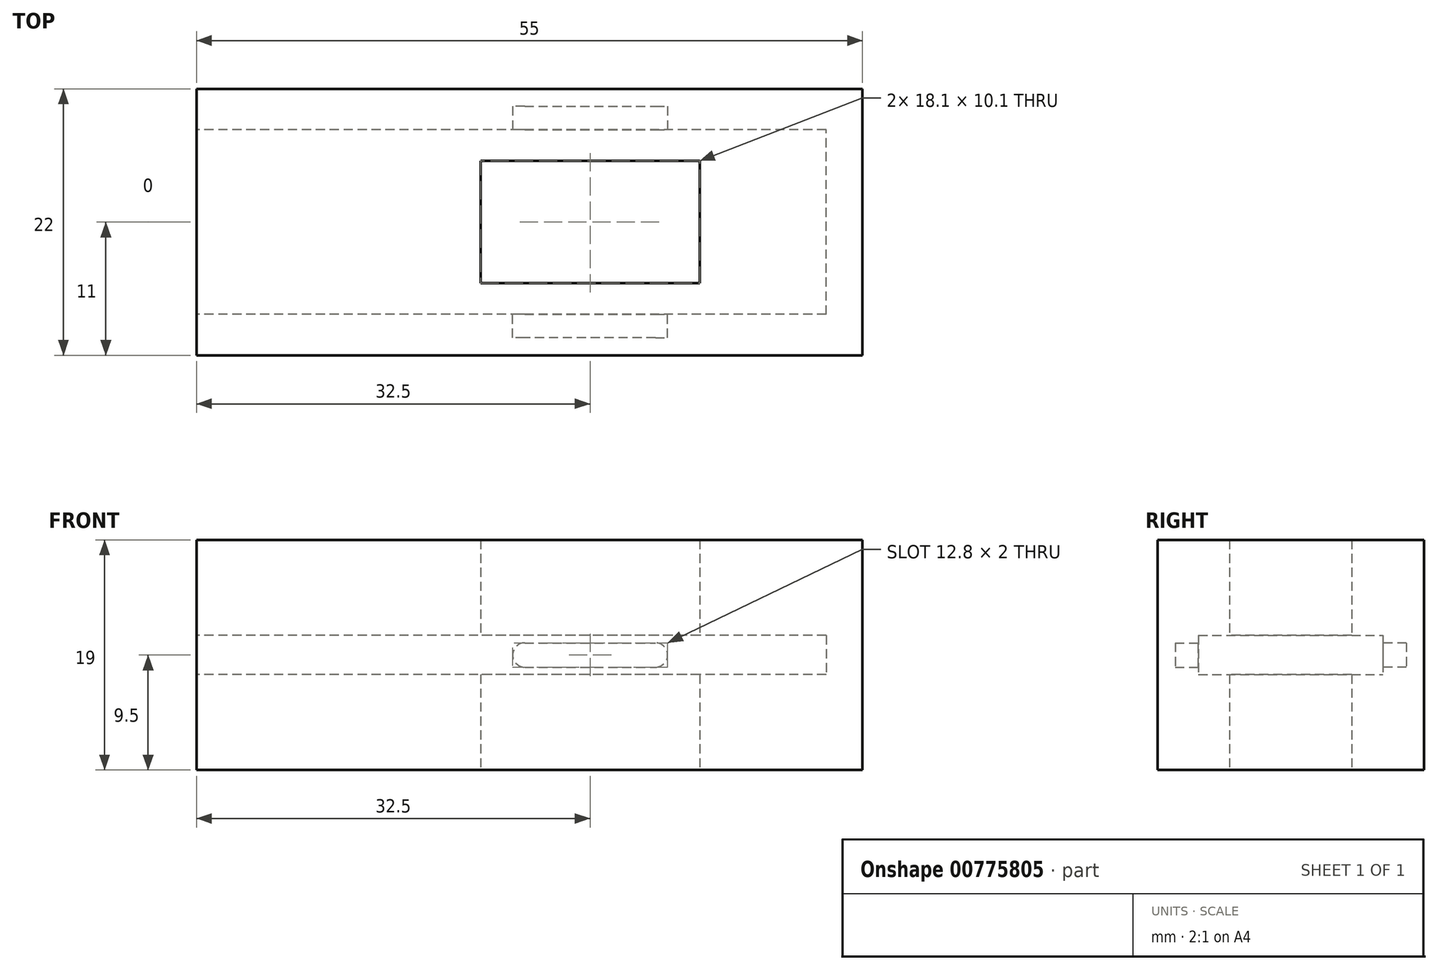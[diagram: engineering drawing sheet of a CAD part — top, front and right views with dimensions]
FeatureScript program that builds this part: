
annotation { "Feature Type Name" : "Feature", "Feature Type Description" : "" }
export const myFeature = defineFeature(function(context is Context, id is Id, definition is map)
    precondition{}
    {
        {
            var Q0;
            Q0=qCreatedBy(makeId("Front.planeOp"),FACE);
            var sketch = newSketch(context, id + "F0", { "sketchPlane" : qUnion([Q0])});
            skLineSegment(sketch, "E0.bottom", {"start": v(-27.5, 9.5) * mm, "end": v(27.5, 9.5) * mm});
            skLineSegment(sketch, "E0.top", {"start": v(-27.5, -9.5) * mm, "end": v(27.5, -9.5) * mm});
            skLineSegment(sketch, "E0.left", {"start": v(-27.5, 9.5) * mm, "end": v(-27.5, -9.5) * mm});
            skLineSegment(sketch, "E0.right", {"start": v(27.5, 9.5) * mm, "end": v(27.5, -9.5) * mm});
            skPoint(sketch, "E0.middle", {"position": v(0, 0) * mm});
            skPoint(sketch, "E1", {"position": v(5, 0) * mm});
            skSolve(sketch);
        }
        {
            var Q0;
            Q0=makeQuery(id+"F0.imprint","IMPRINT",FACE,{"disambiguationData":[TD([[makeQuery(id+"F0.imprint","IMPRINT",EDGE,{"derivedFrom":sQuery(id+"F0.wireOp",EDGE,"E0.bottom")}),-1.0]])]});
            extrude(context, id + "F1", {"entities" : qUnion([Q0]), "endBound" : BoundingType.SYMMETRIC, "depth" : 22 * mm, "offsetDistance" : 25 * mm});
        }
        {
            var Q0;
            Q0=qCreatedBy(makeId("Top.planeOp"),FACE);
            var sketch = newSketch(context, id + "F2", { "sketchPlane" : qUnion([Q0])});
            skLineSegment(sketch, "E2.bottom", {"start": v(14.05, 5.05) * mm, "end": v(-4.05, 5.05) * mm});
            skLineSegment(sketch, "E2.top", {"start": v(14.05, -5.05) * mm, "end": v(-4.05, -5.05) * mm});
            skLineSegment(sketch, "E2.left", {"start": v(14.05, 5.05) * mm, "end": v(14.05, -5.05) * mm});
            skLineSegment(sketch, "E2.right", {"start": v(-4.05, 5.05) * mm, "end": v(-4.05, -5.05) * mm});
            skPoint(sketch, "E2.middle", {"position": v(5, 0) * mm});
            skSolve(sketch);
        }
        {
            var Q0;
            Q0 = qSketchRegion(id + "F2", true);
            extrude(context, id + "F3", {"entities" : qUnion([Q0]), "operationType" : NewBodyOperationType.REMOVE, "endBound" : BoundingType.SYMMETRIC, "depth" : 22 * mm, "offsetDistance" : 25 * mm});
        }
        {
            var Q0;
            Q0=makeQuery(id+"F3.boolean.opBoolean","COPY",FACE,{"derivedFrom":makeQuery(id+"F3.opExtrude","SWEPT_FACE",FACE,{"disambiguationData":[OSD([sQuery(id+"F2.wireOp",EDGE,"E2.bottom")])]})});
            var sketch = newSketch(context, id + "F4", { "sketchPlane" : qUnion([Q0])});
            skPoint(sketch, "E3", {"position": v(5, 0) * mm});
            skPoint(sketch, "E4", {"position": v(-0.4, 0) * mm});
            skPoint(sketch, "E5", {"position": v(10.4, 0) * mm});
            skLineSegment(sketch, "E6", {"start": v(-0.4, 1) * mm, "end": v(10.4, 1) * mm});
            skLineSegment(sketch, "E7", {"start": v(-0.4, -1) * mm, "end": v(10.4, -1) * mm});
            skArc(sketch, "E8", {"start": v(-0.4, 1) * mm, "mid": v(-1.4, 0) * mm, "end": v(-0.4, -1) * mm});
            skArc(sketch, "E9", {"start": v(10.4, -1) * mm, "mid": v(11.4, 0) * mm, "end": v(10.4, 1) * mm});
            skSolve(sketch);
        }
        {
            var Q0;
            Q0=makeQuery(id+"F4.imprint","IMPRINT",FACE,{"disambiguationData":[TD([[makeQuery(id+"F4.imprint","IMPRINT",EDGE,{"derivedFrom":sQuery(id+"F4.wireOp",EDGE,"E6")}),-1.0]])]});
            extrude(context, id + "F5", {"entities" : qUnion([Q0]), "operationType" : NewBodyOperationType.REMOVE, "oppositeDirection" : true, "depth" : 4.5 * mm, "offsetDistance" : 25 * mm});
        }
        {
            var Q0;
            Q0=makeQuery(id+"F3.boolean.opBoolean","COPY",FACE,{"derivedFrom":makeQuery(id+"F3.opExtrude","SWEPT_FACE",FACE,{"disambiguationData":[OSD([sQuery(id+"F2.wireOp",EDGE,"E2.top")])]})});
            var sketch = newSketch(context, id + "F6", { "sketchPlane" : qUnion([Q0])});
            skPoint(sketch, "E10", {"position": v(0.4, 0) * mm});
            skPoint(sketch, "E11", {"position": v(-5, 0) * mm});
            skPoint(sketch, "E12", {"position": v(-10.4, 0) * mm});
            skLineSegment(sketch, "E13", {"start": v(-10.4, -1) * mm, "end": v(0.4, -1) * mm});
            skLineSegment(sketch, "E14", {"start": v(-10.4, 1) * mm, "end": v(0.4, 1) * mm});
            skArc(sketch, "E15", {"start": v(-10.4, 1) * mm, "mid": v(-11.4, 0) * mm, "end": v(-10.4, -1) * mm});
            skArc(sketch, "E16", {"start": v(0.4, -1) * mm, "mid": v(1.4, 0) * mm, "end": v(0.4, 1) * mm});
            skSolve(sketch);
        }
        {
            var Q0;
            Q0=makeQuery(id+"F6.imprint","IMPRINT",FACE,{"disambiguationData":[TD([[makeQuery(id+"F6.imprint","IMPRINT",EDGE,{"derivedFrom":sQuery(id+"F6.wireOp",EDGE,"E13")}),1.0]])]});
            extrude(context, id + "F7", {"entities" : qUnion([Q0]), "operationType" : NewBodyOperationType.REMOVE, "oppositeDirection" : true, "depth" : 4.5 * mm, "offsetDistance" : 25 * mm});
        }
        {
            var Q0;
            Q0=makeQuery(id+"F1.opExtrude","SWEPT_FACE",FACE,{"disambiguationData":[OSD([sQuery(id+"F0.wireOp",EDGE,"E0.left")])]});
            var sketch = newSketch(context, id + "F8", { "sketchPlane" : qUnion([Q0])});
            skLineSegment(sketch, "E17.bottom", {"start": v(7.62, 1.63) * mm, "end": v(-7.63, 1.63) * mm});
            skLineSegment(sketch, "E17.top", {"start": v(7.62, -1.63) * mm, "end": v(-7.63, -1.63) * mm});
            skLineSegment(sketch, "E17.left", {"start": v(7.62, 1.63) * mm, "end": v(7.62, -1.63) * mm});
            skLineSegment(sketch, "E17.right", {"start": v(-7.63, 1.63) * mm, "end": v(-7.63, -1.63) * mm});
            skPoint(sketch, "E17.middle", {"position": v(0, 0) * mm});
            skSolve(sketch);
        }
        {
            var Q0;
            Q0=makeQuery(id+"F8.imprint","IMPRINT",FACE,{"disambiguationData":[TD([[makeQuery(id+"F8.imprint","IMPRINT",EDGE,{"derivedFrom":sQuery(id+"F8.wireOp",EDGE,"E17.bottom")}),1.0]])]});
            extrude(context, id + "F9", {"entities" : qUnion([Q0]), "operationType" : NewBodyOperationType.REMOVE, "oppositeDirection" : true, "depth" : 52 * mm, "offsetDistance" : 25 * mm});
        }
    });
